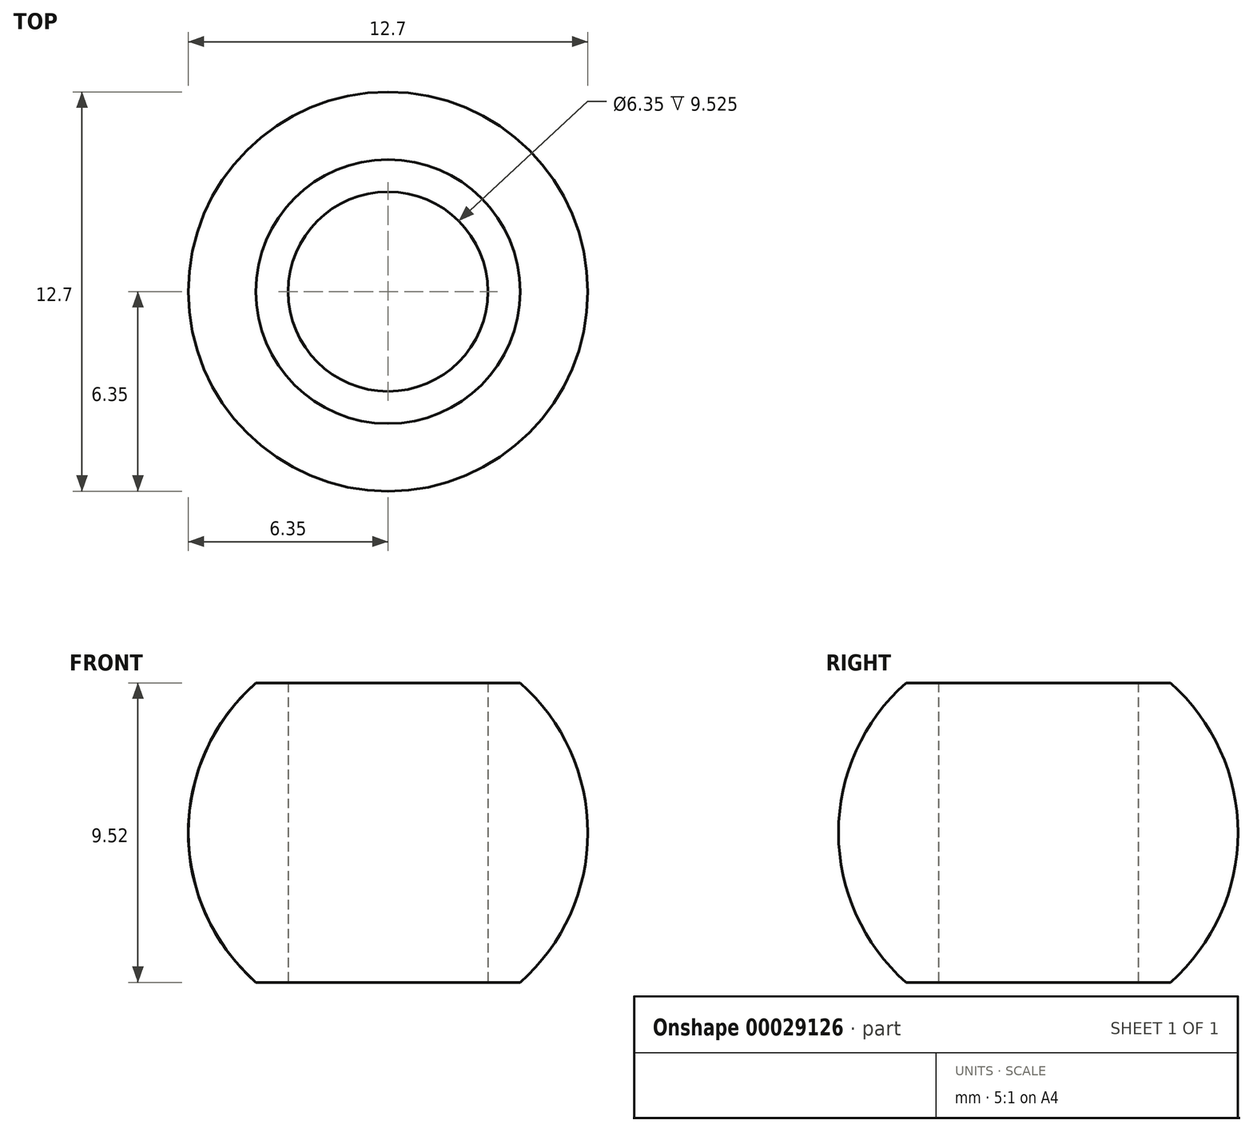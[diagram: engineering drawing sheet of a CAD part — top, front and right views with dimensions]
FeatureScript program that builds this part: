
annotation { "Feature Type Name" : "Feature", "Feature Type Description" : "" }
export const myFeature = defineFeature(function(context is Context, id is Id, definition is map)
    precondition{}
    {
        {
            var Q0;
            Q0=qCreatedBy(makeId("Top.planeOp"),FACE);
            var sketch = newSketch(context, id + "F0", { "sketchPlane" : qUnion([Q0])});
            skLineSegment(sketch, "E0", {"start": v(0, 0) * mm, "end": v(0, -41.28) * mm, "construction": true});
            skLineSegment(sketch, "E1", {"start": v(0, -41.28) * mm, "end": v(3.18, -41.28) * mm});
            skLineSegment(sketch, "E2", {"start": v(3.18, -41.28) * mm, "end": v(3.18, -15.95) * mm});
            skArc(sketch, "E3.MirrorCS", {"start": v(9.22, -2.4) * mm, "mid": v(7.57, -7.41) * mm, "end": v(4.7, -11.83) * mm});
            skArc(sketch, "E4.filletArc", {"start": v(4.7, -11.83) * mm, "mid": v(3.57, -13.76) * mm, "end": v(3.18, -15.95) * mm});
            skLineSegment(sketch, "E5", {"start": v(0, -41.28) * mm, "end": v(0, 9.53) * mm});
            skArc(sketch, "E6", {"start": v(9.22, -2.4) * mm, "mid": v(7.54, 5.82) * mm, "end": v(0, 9.53) * mm});
            skSolve(sketch);
        }
        {
            var Q0;
            Q0=qCreatedBy(makeId("Right.planeOp"),FACE);
            var sketch = newSketch(context, id + "F1", { "sketchPlane" : qUnion([Q0])});
            skLineSegment(sketch, "E7", {"start": v(3.18, 0) * mm, "end": v(3.18, 4.76) * mm});
            skArc(sketch, "E8", {"start": v(4.2, -4.76) * mm, "mid": v(6.35, 0) * mm, "end": v(4.2, 4.76) * mm});
            skLineSegment(sketch, "E9.MirrorCS", {"start": v(3.18, 0) * mm, "end": v(3.18, -4.76) * mm});
            skArc(sketch, "E10.MirrorC", {"start": v(4.2, 4.76) * mm, "mid": v(6.35, 0) * mm, "end": v(4.2, -4.76) * mm});
            skLineSegment(sketch, "E11", {"start": v(3.18, -4.76) * mm, "end": v(4.2, -4.76) * mm});
            skLineSegment(sketch, "E12", {"start": v(3.18, 4.76) * mm, "end": v(4.2, 4.76) * mm});
            skLineSegment(sketch, "E13", {"start": v(0, 0) * mm, "end": v(0, 16.54) * mm});
            skSolve(sketch);
        }
        {
            var Q0;
            Q0 = qSketchRegion(id + "F1", true);
            var Q1;
            Q1=sQuery(id+"F1.wireOp",EDGE,"E13");
            revolve(context, id + "F2", {"entities" : qUnion([Q0]), "axis" : qUnion([Q1]), "revolveType" : RevolveType.FULL});
        }
        {
            var Q0;
            Q0 = qSketchRegion(id + "F0", true);
            var Q1;
            Q1=sQuery(id+"F0.wireOp",EDGE,"E5");
            revolve(context, id + "F3", {"operationType" : NewBodyOperationType.ADD, "entities" : qUnion([Q0]), "axis" : qUnion([Q1]), "revolveType" : RevolveType.FULL});
        }
        {
            var Q0;
            Q0=qCreatedBy(makeId("Right.planeOp"),FACE);
            var sketch = newSketch(context, id + "F4", { "sketchPlane" : qUnion([Q0])});
            skLineSegment(sketch, "E14", {"start": v(-14.79, 3.57) * mm, "end": v(8.83, 3.57) * mm});
            skLineSegment(sketch, "E15.MirrorCS", {"start": v(-14.79, -3.57) * mm, "end": v(8.83, -3.57) * mm});
            skLineSegment(sketch, "E16", {"start": v(-14.79, 3.57) * mm, "end": v(-14.79, 13.82) * mm});
            skLineSegment(sketch, "E17", {"start": v(-14.79, 13.82) * mm, "end": v(8.39, 13.82) * mm});
            skLineSegment(sketch, "E18", {"start": v(8.39, 13.82) * mm, "end": v(8.83, 3.57) * mm});
            skLineSegment(sketch, "E19", {"start": v(8.83, -3.57) * mm, "end": v(8.83, -14.01) * mm});
            skLineSegment(sketch, "E20", {"start": v(8.83, -14.01) * mm, "end": v(-14.79, -14.01) * mm});
            skLineSegment(sketch, "E21", {"start": v(-14.79, -14.01) * mm, "end": v(-14.79, -3.57) * mm});
            skSolve(sketch);
        }
        {
            var Q0;
            Q0 = qSketchRegion(id + "F4", true);
            extrude(context, id + "F5", {"entities" : qUnion([Q0]), "operationType" : NewBodyOperationType.REMOVE, "endBound" : BoundingType.SYMMETRIC, "oppositeDirection" : true, "depth" : 25.4 * mm});
        }
        {
            var Q0;
            Q0 = qSketchRegion(id + "F1", true);
            var Q1;
            Q1=sQuery(id+"F1.wireOp",EDGE,"E13");
            revolve(context, id + "F6", {"operationType" : NewBodyOperationType.REMOVE, "entities" : qUnion([Q0]), "axis" : qUnion([Q1]), "revolveType" : RevolveType.FULL, "oppositeDirection" : true});
        }
        {
            var Q0;
            Q0 = qSketchRegion(id + "F1", true);
            var Q1;
            Q1=sQuery(id+"F1.wireOp",EDGE,"E13");
            revolve(context, id + "F7", {"entities" : qUnion([Q0]), "axis" : qUnion([Q1]), "revolveType" : RevolveType.FULL});
        }
        {
            var Q0;
            Q0=makeQuery(id+"F3.opRevolve","SWEPT_EDGE",EDGE,{"disambiguationData":[OSD([sQuery(id+"F0.wireOp",EDGE,"E1"),sQuery(id+"F0.wireOp",EDGE,"E2")])]});
            chamfer(context, id + "F8", {"entities" : qUnion([Q0]), "width" : 0.76 * mm, "tangentPropagation" : true});
        }
        {
            var Q0;
            Q0=makeQuery(id+"F6.boolean.opBoolean","SPLIT",BODY,{"disambiguationData":[OD(1.0)],"derivedFrom":makeQuery(id+"F2.opRevolve","SWEPT_BODY",BODY,{"disambiguationData":[OSD([sQuery(id+"F1.wireOp",EDGE,"E7"),sQuery(id+"F1.wireOp",EDGE,"E9.MirrorCS"),sQuery(id+"F1.wireOp",EDGE,"E10.MirrorC"),sQuery(id+"F1.wireOp",EDGE,"E11"),sQuery(id+"F1.wireOp",EDGE,"E12")])]})});
            deleteBodies(context, id + "F9", {"entities" : qUnion([Q0])});
        }
    });
